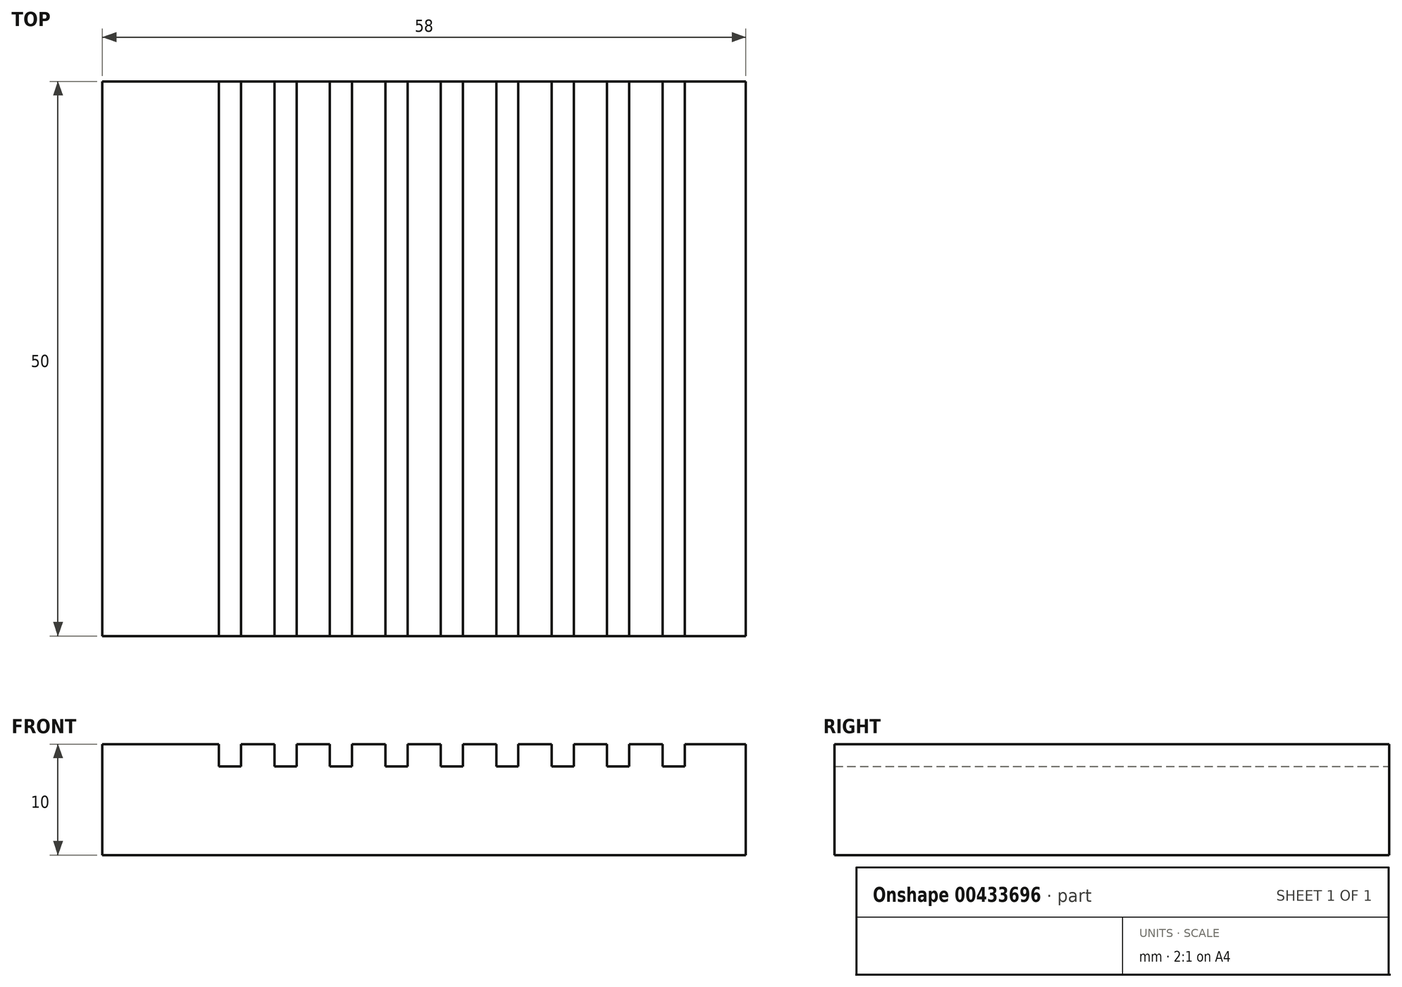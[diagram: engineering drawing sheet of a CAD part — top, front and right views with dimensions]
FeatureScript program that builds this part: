
annotation { "Feature Type Name" : "Feature", "Feature Type Description" : "" }
export const myFeature = defineFeature(function(context is Context, id is Id, definition is map)
    precondition{}
    {
        {
            var Q0;
            Q0=qCreatedBy(makeId("Top.planeOp"),FACE);
            var sketch = newSketch(context, id + "F0", { "sketchPlane" : qUnion([Q0])});
            skLineSegment(sketch, "E0.bottom", {"start": v(29, 25) * mm, "end": v(-29, 25) * mm});
            skLineSegment(sketch, "E0.top", {"start": v(29, -25) * mm, "end": v(-29, -25) * mm});
            skLineSegment(sketch, "E0.left", {"start": v(29, 25) * mm, "end": v(29, -25) * mm});
            skLineSegment(sketch, "E0.right", {"start": v(-29, 25) * mm, "end": v(-29, -25) * mm});
            skPoint(sketch, "E0.middle", {"position": v(0, 0) * mm});
            skLineSegment(sketch, "E1.bottom", {"start": v(-23.5, -25) * mm, "end": v(-21.5, -25) * mm});
            skLineSegment(sketch, "E1.top", {"start": v(-23.5, 25) * mm, "end": v(-21.5, 25) * mm});
            skLineSegment(sketch, "E1.left", {"start": v(-23.5, -25) * mm, "end": v(-23.5, 25) * mm});
            skLineSegment(sketch, "E1.right", {"start": v(-21.5, -25) * mm, "end": v(-21.5, 25) * mm});
            skLineSegment(sketch, "E2.1.0.0", {"start": v(-16.5, -25) * mm, "end": v(-16.5, 25) * mm});
            skLineSegment(sketch, "E2.1.0.1", {"start": v(-18.5, -25) * mm, "end": v(-18.5, 25) * mm});
            skLineSegment(sketch, "E2.1.0.2", {"start": v(-18.5, 25) * mm, "end": v(-16.5, 25) * mm});
            skLineSegment(sketch, "E2.1.0.3", {"start": v(-18.5, -25) * mm, "end": v(-16.5, -25) * mm});
            skLineSegment(sketch, "E2.2.0.0", {"start": v(-11.5, -25) * mm, "end": v(-11.5, 25) * mm});
            skLineSegment(sketch, "E2.2.0.1", {"start": v(-13.5, -25) * mm, "end": v(-13.5, 25) * mm});
            skLineSegment(sketch, "E2.2.0.2", {"start": v(-13.5, 25) * mm, "end": v(-11.5, 25) * mm});
            skLineSegment(sketch, "E2.2.0.3", {"start": v(-13.5, -25) * mm, "end": v(-11.5, -25) * mm});
            skLineSegment(sketch, "E2.3.0.0", {"start": v(-6.5, -25) * mm, "end": v(-6.5, 25) * mm});
            skLineSegment(sketch, "E2.3.0.1", {"start": v(-8.5, -25) * mm, "end": v(-8.5, 25) * mm});
            skLineSegment(sketch, "E2.3.0.2", {"start": v(-8.5, 25) * mm, "end": v(-6.5, 25) * mm});
            skLineSegment(sketch, "E2.3.0.3", {"start": v(-8.5, -25) * mm, "end": v(-6.5, -25) * mm});
            skLineSegment(sketch, "E2.4.0.0", {"start": v(-1.5, -25) * mm, "end": v(-1.5, 25) * mm});
            skLineSegment(sketch, "E2.4.0.1", {"start": v(-3.5, -25) * mm, "end": v(-3.5, 25) * mm});
            skLineSegment(sketch, "E2.4.0.2", {"start": v(-3.5, 25) * mm, "end": v(-1.5, 25) * mm});
            skLineSegment(sketch, "E2.4.0.3", {"start": v(-3.5, -25) * mm, "end": v(-1.5, -25) * mm});
            skLineSegment(sketch, "E2.5.0.0", {"start": v(3.5, -25) * mm, "end": v(3.5, 25) * mm});
            skLineSegment(sketch, "E2.5.0.1", {"start": v(1.5, -25) * mm, "end": v(1.5, 25) * mm});
            skLineSegment(sketch, "E2.5.0.2", {"start": v(1.5, 25) * mm, "end": v(3.5, 25) * mm});
            skLineSegment(sketch, "E2.5.0.3", {"start": v(1.5, -25) * mm, "end": v(3.5, -25) * mm});
            skLineSegment(sketch, "E2.6.0.0", {"start": v(8.5, -25) * mm, "end": v(8.5, 25) * mm});
            skLineSegment(sketch, "E2.6.0.1", {"start": v(6.5, -25) * mm, "end": v(6.5, 25) * mm});
            skLineSegment(sketch, "E2.6.0.2", {"start": v(6.5, 25) * mm, "end": v(8.5, 25) * mm});
            skLineSegment(sketch, "E2.6.0.3", {"start": v(6.5, -25) * mm, "end": v(8.5, -25) * mm});
            skLineSegment(sketch, "E2.7.0.0", {"start": v(13.5, -25) * mm, "end": v(13.5, 25) * mm});
            skLineSegment(sketch, "E2.7.0.1", {"start": v(11.5, -25) * mm, "end": v(11.5, 25) * mm});
            skLineSegment(sketch, "E2.7.0.2", {"start": v(11.5, 25) * mm, "end": v(13.5, 25) * mm});
            skLineSegment(sketch, "E2.7.0.3", {"start": v(11.5, -25) * mm, "end": v(13.5, -25) * mm});
            skLineSegment(sketch, "E2.8.0.0", {"start": v(18.5, -25) * mm, "end": v(18.5, 25) * mm});
            skLineSegment(sketch, "E2.8.0.1", {"start": v(16.5, -25) * mm, "end": v(16.5, 25) * mm});
            skLineSegment(sketch, "E2.8.0.2", {"start": v(16.5, 25) * mm, "end": v(18.5, 25) * mm});
            skLineSegment(sketch, "E2.8.0.3", {"start": v(16.5, -25) * mm, "end": v(18.5, -25) * mm});
            skLineSegment(sketch, "E2.9.0.0", {"start": v(23.5, -25) * mm, "end": v(23.5, 25) * mm});
            skLineSegment(sketch, "E2.9.0.1", {"start": v(21.5, -25) * mm, "end": v(21.5, 25) * mm});
            skLineSegment(sketch, "E2.9.0.2", {"start": v(21.5, 25) * mm, "end": v(23.5, 25) * mm});
            skLineSegment(sketch, "E2.9.0.3", {"start": v(21.5, -25) * mm, "end": v(23.5, -25) * mm});
            skLineSegment(sketch, "E2.direction1", {"start": v(-23.5, -25) * mm, "end": v(-18.5, -25) * mm, "construction": true});
            skSolve(sketch);
        }
        {
            var Q0;
            Q0 = qSketchRegion(id + "F0", true);
            extrude(context, id + "F1", {"entities" : qUnion([Q0]), "oppositeDirection" : true, "depth" : 10 * mm});
        }
        {
            var Q0;
            Q0=makeQuery(id+"F0.imprint","IMPRINT",FACE,{"disambiguationData":[TD([[makeQuery(id+"F0.imprint","IMPRINT",EDGE,{"derivedFrom":sQuery(id+"F0.wireOp",EDGE,"E1.bottom")}),1.0]])]});
            var Q1;
            Q1=makeQuery(id+"F0.imprint","IMPRINT",FACE,{"disambiguationData":[TD([[makeQuery(id+"F0.imprint","IMPRINT",EDGE,{"derivedFrom":sQuery(id+"F0.wireOp",EDGE,"E2.1.0.0")}),1.0]])]});
            var Q2;
            Q2=makeQuery(id+"F0.imprint","IMPRINT",FACE,{"disambiguationData":[TD([[makeQuery(id+"F0.imprint","IMPRINT",EDGE,{"derivedFrom":sQuery(id+"F0.wireOp",EDGE,"E2.2.0.0")}),1.0]])]});
            var Q3;
            Q3=makeQuery(id+"F0.imprint","IMPRINT",FACE,{"disambiguationData":[TD([[makeQuery(id+"F0.imprint","IMPRINT",EDGE,{"derivedFrom":sQuery(id+"F0.wireOp",EDGE,"E2.3.0.0")}),1.0]])]});
            var Q4;
            Q4=makeQuery(id+"F0.imprint","IMPRINT",FACE,{"disambiguationData":[TD([[makeQuery(id+"F0.imprint","IMPRINT",EDGE,{"derivedFrom":sQuery(id+"F0.wireOp",EDGE,"E2.4.0.0")}),1.0]])]});
            var Q5;
            Q5=makeQuery(id+"F0.imprint","IMPRINT",FACE,{"disambiguationData":[TD([[makeQuery(id+"F0.imprint","IMPRINT",EDGE,{"derivedFrom":sQuery(id+"F0.wireOp",EDGE,"E2.5.0.0")}),1.0]])]});
            var Q6;
            Q6=makeQuery(id+"F0.imprint","IMPRINT",FACE,{"disambiguationData":[TD([[makeQuery(id+"F0.imprint","IMPRINT",EDGE,{"derivedFrom":sQuery(id+"F0.wireOp",EDGE,"E2.6.0.0")}),1.0]])]});
            var Q7;
            Q7=makeQuery(id+"F0.imprint","IMPRINT",FACE,{"disambiguationData":[TD([[makeQuery(id+"F0.imprint","IMPRINT",EDGE,{"derivedFrom":sQuery(id+"F0.wireOp",EDGE,"E2.7.0.0")}),1.0]])]});
            var Q8;
            Q8=makeQuery(id+"F0.imprint","IMPRINT",FACE,{"disambiguationData":[TD([[makeQuery(id+"F0.imprint","IMPRINT",EDGE,{"derivedFrom":sQuery(id+"F0.wireOp",EDGE,"E2.8.0.0")}),1.0]])]});
            var Q9;
            Q9=makeQuery(id+"F0.imprint","IMPRINT",FACE,{"disambiguationData":[TD([[makeQuery(id+"F0.imprint","IMPRINT",EDGE,{"derivedFrom":sQuery(id+"F0.wireOp",EDGE,"E2.9.0.0")}),1.0]])]});
            extrude(context, id + "F2", {"entities" : qUnion([Q0, Q1, Q2, Q3, Q4, Q5, Q6, Q7, Q8, Q9]), "operationType" : NewBodyOperationType.REMOVE, "oppositeDirection" : true, "depth" : 2 * mm});
        }
    });
